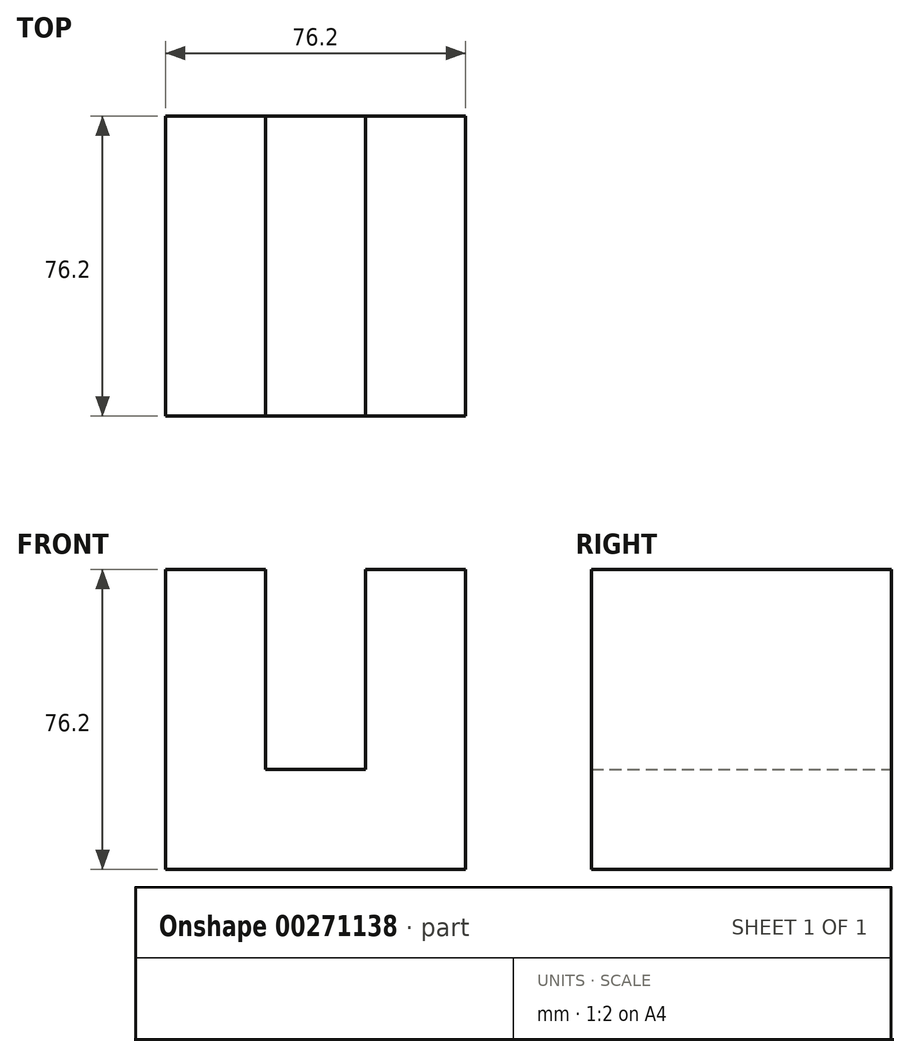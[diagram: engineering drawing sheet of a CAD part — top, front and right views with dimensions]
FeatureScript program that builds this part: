
annotation { "Feature Type Name" : "Feature", "Feature Type Description" : "" }
export const myFeature = defineFeature(function(context is Context, id is Id, definition is map)
    precondition{}
    {
        {
            var Q0;
            Q0=qCreatedBy(makeId("Front.planeOp"),FACE);
            var sketch = newSketch(context, id + "F0", { "sketchPlane" : qUnion([Q0])});
            skLineSegment(sketch, "E0", {"start": v(-37.24, -42.96) * mm, "end": v(-37.24, 33.24) * mm});
            skLineSegment(sketch, "E1", {"start": v(-37.24, 33.24) * mm, "end": v(-11.84, 33.24) * mm});
            skLineSegment(sketch, "E2", {"start": v(-11.84, 33.24) * mm, "end": v(-11.84, -17.56) * mm});
            skLineSegment(sketch, "E3", {"start": v(-11.84, -17.56) * mm, "end": v(13.56, -17.56) * mm});
            skLineSegment(sketch, "E4", {"start": v(13.56, -17.56) * mm, "end": v(13.56, 33.24) * mm});
            skLineSegment(sketch, "E5", {"start": v(13.56, 33.24) * mm, "end": v(38.96, 33.24) * mm});
            skLineSegment(sketch, "E6", {"start": v(38.96, 33.24) * mm, "end": v(38.96, -17.56) * mm});
            skLineSegment(sketch, "E7", {"start": v(38.96, -17.56) * mm, "end": v(38.96, -42.96) * mm});
            skLineSegment(sketch, "E8", {"start": v(38.96, -42.96) * mm, "end": v(-37.24, -42.96) * mm});
            skSolve(sketch);
        }
        {
            var Q0;
            Q0 = qSketchRegion(id + "F0", true);
            extrude(context, id + "F1", {"entities" : qUnion([Q0]), "depth" : 76.2 * mm});
        }
    });
